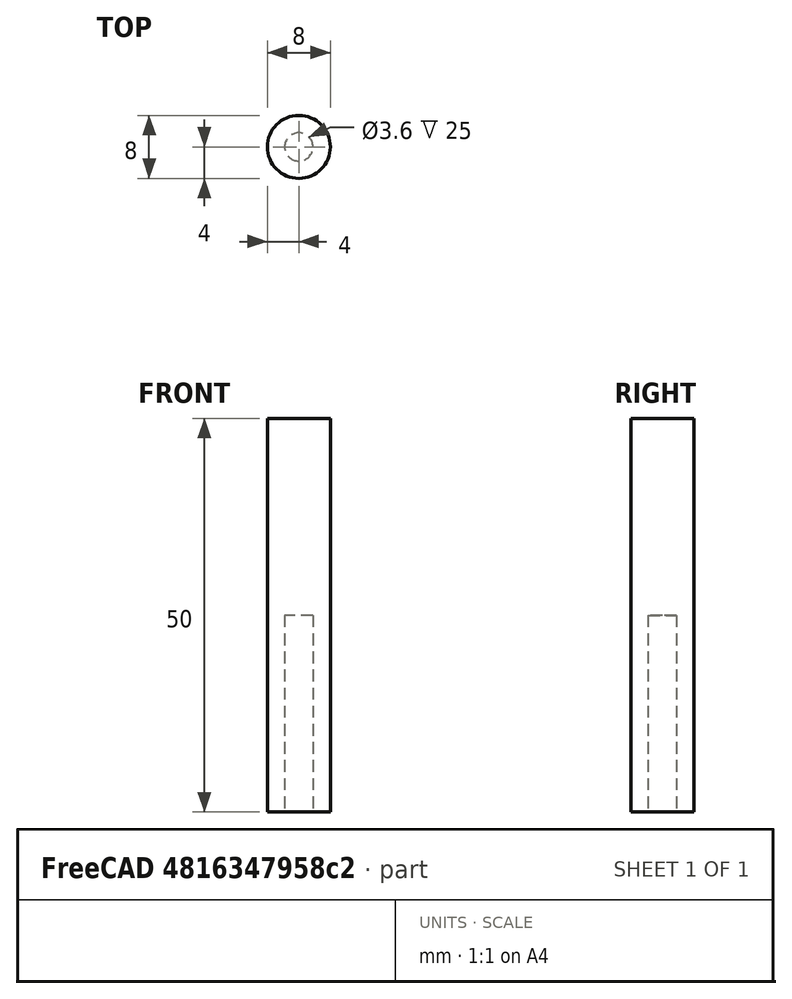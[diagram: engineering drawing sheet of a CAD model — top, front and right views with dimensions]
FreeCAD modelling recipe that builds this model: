
FCSTD DOCUMENT  (FreeCAD 0.19R)
Label: plunger
License: All rights reserved
LicenseURL: http://en.wikipedia.org/wiki/All_rights_reserved
objects: Sketcher::SketchObject×1, PartDesign::Revolution×1, PartDesign::Body×1
note: 4 computed .brp shape members not serialized (recipe doc carries the construction recipe); baked Part::Feature solids carry a one-line shape summary decoded from their .brp

FEATURE [Sketcher::SketchObject] Sketch
  FullyConstrained = true
  MapMode = 5
  Placement = pos=(0,0,0) rot=(1,0,0;1.5708rad)
  Support = -> [XZ_Plane]
  sketch-geometry (6):
    g0: LineSegment StartX=0 StartY=50 StartZ=0 EndX=0 EndY=25 EndZ=0
    g1: LineSegment StartX=0 StartY=25 StartZ=0 EndX=1.8 EndY=25 EndZ=0
    g2: LineSegment StartX=1.8 StartY=25 StartZ=0 EndX=1.8 EndY=0 EndZ=0
    g3: LineSegment StartX=1.8 StartY=0 StartZ=0 EndX=4 EndY=0 EndZ=0
    g4: LineSegment StartX=4 StartY=0 StartZ=0 EndX=4 EndY=50 EndZ=0
    g5: LineSegment StartX=4 StartY=50 StartZ=0 EndX=0 EndY=50 EndZ=0
  constraints (18):
    c: Vertical(g0)
    c: Coincident(g0,g1)
    c: Horizontal(g1)
    c: Coincident(g1,g2)
    c: Vertical(g2)
    c: Coincident(g2,g3)
    c: Coincident(g3,g4)
    c: Vertical(g4)
    c: Coincident(g4,g5)
    c: Coincident(g5,g0)
    c: Vertical(g-1,g0)
    c: Horizontal(g5)
    c: Horizontal(g3)
    c: DistanceX(g1,g1) = 1.8
    c: DistanceX(g5,g5) = 4
    c: Horizontal(g2,g-1)
    c: DistanceY(g-1,g0) = 50
    c: DistanceY(g-1,g0) = 25
FEATURE [PartDesign::Revolution] Revolution
  Angle = 360
  Axis = (0,2e-16,1)
  Base = (0,0,0)
  Placement = pos=(0,0,0) rot=(1,0,0;1.5708rad)
  Profile = -> Sketch
  ReferenceAxis = -> Sketch [V_Axis]
  Reversed = true
FEATURE [PartDesign::Body] Body
  Group = -> [Sketch,Revolution]
  Origin = -> Origin
  Tip = -> Revolution
